# Revit family: Faucet-Handle-KOHLER-COMPONENTS-K-77963T
name_source: partatom
category: Plumbing Fixtures
revit_build: Autodesk Revit 2017 (Build: 20160225_1515(x64)
units: mm (PartAtom-declared; Revit-internal decimal feet)

## family parameters
Cut with Voids When Loaded = No
Host = Face
OmniClass Number = 23.31.11.00
OmniClass Title = Faucets
Part Type = Normal
Room Calculation Point = No
Round Connector Dimension = Use Diameter
Shared = No

## types (12) — shared parameters
ADA Compliant = No
Assembly Code = D2010
CW Connection = Yes
Cold Water Inlet = Cold Water Inlet
Date Modified = 08/31/2020
Default Elevation = 36"
Drain Included = No
Flow Rate = 0 GPM
HW Connection = Yes
Handle Clearance = 1 3/16"
Height = 1 3/16"
Hot Water Inlet = Hot Water Inlet
Length = 2 3/8"
Manufacturer = KOHLER Co.
Master Format 2014 = 22 41 39
Master Format 2014 Name = Residential Faucets, Supplies, and Trim
Material = Metal construction
Pressure = 0.00 psi
Product Name = COMPONENTS
URL = http://www.kohler.com.cn
Vent Connection = No
Waste Connection = No
Waste Water Outlet = Waste Water Outlet
WaterSense Certified = No
Width = 2 3/8"

## per-type parameters (varying)
| type | Description | Finish | Model | Product Documentation Link | Product Page URL | Type |
| 8A, AF- Flange Gold | Yiting washbasin faucet push-control knob | Kohler-Metal-AF-Flange_Gold | K-77963T-8A-AF | https://files.kohler.com.cn | https://www.kohler.com.cn | 1 |
| 8A,BN- Roman Silver | Yiting washbasin faucet push-control knob | Kohler-Metal-BN-Roman_Silver | K-77963T-8A-BN | https://files.kohler.com.cn | https://www.kohler.com.cn | 2 |
| 8A, RGD- Rose Gold | Yiting washbasin faucet push-control knob | Kohler-Metal-RGD-Rose_Gold | K-77963T-8A-RGD | https://files.kohler.com.cn | https://www.kohler.com.cn | 3 |
| 8A,CP- Polished chrome | Yiting washbasin faucet push-control knob | Kohler-Metal-CP-Polished_Chrome | K-77963T-8A-CP | https://files.kohler.com.cn | https://www.kohler.com.cn | 4 |
| 8A, TT- Titanium Silver | Yiting washbasin faucet push-control knob | Kohler-Metal-TT-Titanium_Silver | K-77963T-8A-TT | https://files.kohler.com.cn | https://www.kohler.com.cn | 5 |
| 8A, 2BL- Original Black | Yiting washbasin faucet push-control knob | Kohler-Metal-2BL-Original_Black | K-77963T-8A-2BL | https://files.kohler.com.cn | https://www.kohler.com.cn | 6 |
| 8ADR,AF- Flange Black | COMPONENTS ROCKER HANDLE | Kohler-Metal-AF-Flange_Gold | K-77963T-8ADR-AF |  |  | 7 |
| 8ADR,BN- Roman Silver | COMPONENTS ROCKER HANDLE | Kohler-Metal-BN-Roman_Silver | K-77963T-8ADR-BN |  |  | 8 |
| 8ADR,RGD- Rose Gold | COMPONENTS ROCKER HANDLE | Kohler-Metal-RGD-Rose_Gold | K-77963T-8ADR-RGD |  |  | 9 |
| 8ADR, CP- Polished Chrome | COMPONENTS ROCKER HANDLE | Kohler-Metal-CP-Polished_Chrome | K-77963T-8ADR-CP |  |  | 10 |
| 8ADR, TT- Titanium Silver | COMPONENTS ROCKER HANDLE | Kohler-Metal-TT-Titanium_Silver | K-77963T-8ADR-TT |  |  | 11 |
| 8ADR,2BL- Original Black | COMPONENTS ROCKER HANDLE | Kohler-Metal-2BL-Original_Black | K-77963T-8ADR-2BL |  |  | 12 |

## geometry (parser evidence)
native form markers: Sweep x5
no freeform markers — native parametric forms only
